# Revit family: 26804
name_source: partatom
category: Aparatos sanitarios
revit_build: Autodesk Revit 2017 (Build: 20160225_1515(x64)
units: mm (PartAtom-declared; Revit-internal decimal feet)

## family parameters
Anfitrión = Cara
Compartido = No
Corte con vacíos al cargar = No
Cota de conector redondo = Diámetro de uso
Número OmniClass = 23.45.55.14
Punto de cálculo de habitación = No
Tipo de pieza = Normal
Título OmniClass = Single Faucets

## types (1)
- 26804
    Accionamiento = Mediante pulsador
    CAUDAL = 8 l/min.
    CIERRE = Automático en 10 seg.
    Comentarios de tipo = Cuerpo y pulsador en latón. Piezas inferiores en matieriales resistentes a la corrosión e incrustaciones calcáreas. Cabeza intercambiable. Caño disponible en varias longitudes (bajo pedido). Suministrado con caja para empotrar. Entrada hembra de  1/2".
    Conexión AC = No
    Conexión AF = Sí
    Código de montaje = C1030220
    Descripción = Grifo temporalizado de un agua para instalación mural y apertura por pulsador.
    ENTRADA = Con latiguillo flexible de 1/2"
    Elevación por defecto = 1219 mm
    Fabricante = PRESTO IBÉRICA
    Imagen de tipo = <Ninguno>
    Material = LATON CROMADO
    Modelo = PRESTO XT 2000 - P Inox
    PESO BRUTO = 1,920 Kg
    Presión Máxima = 8 bar
    REFERENCIA = 26804
    TIPO DE AGUA = Fria
    Teléfono = (+34) 915 782 575
    URL = http://www.griferiasgalindo.com
